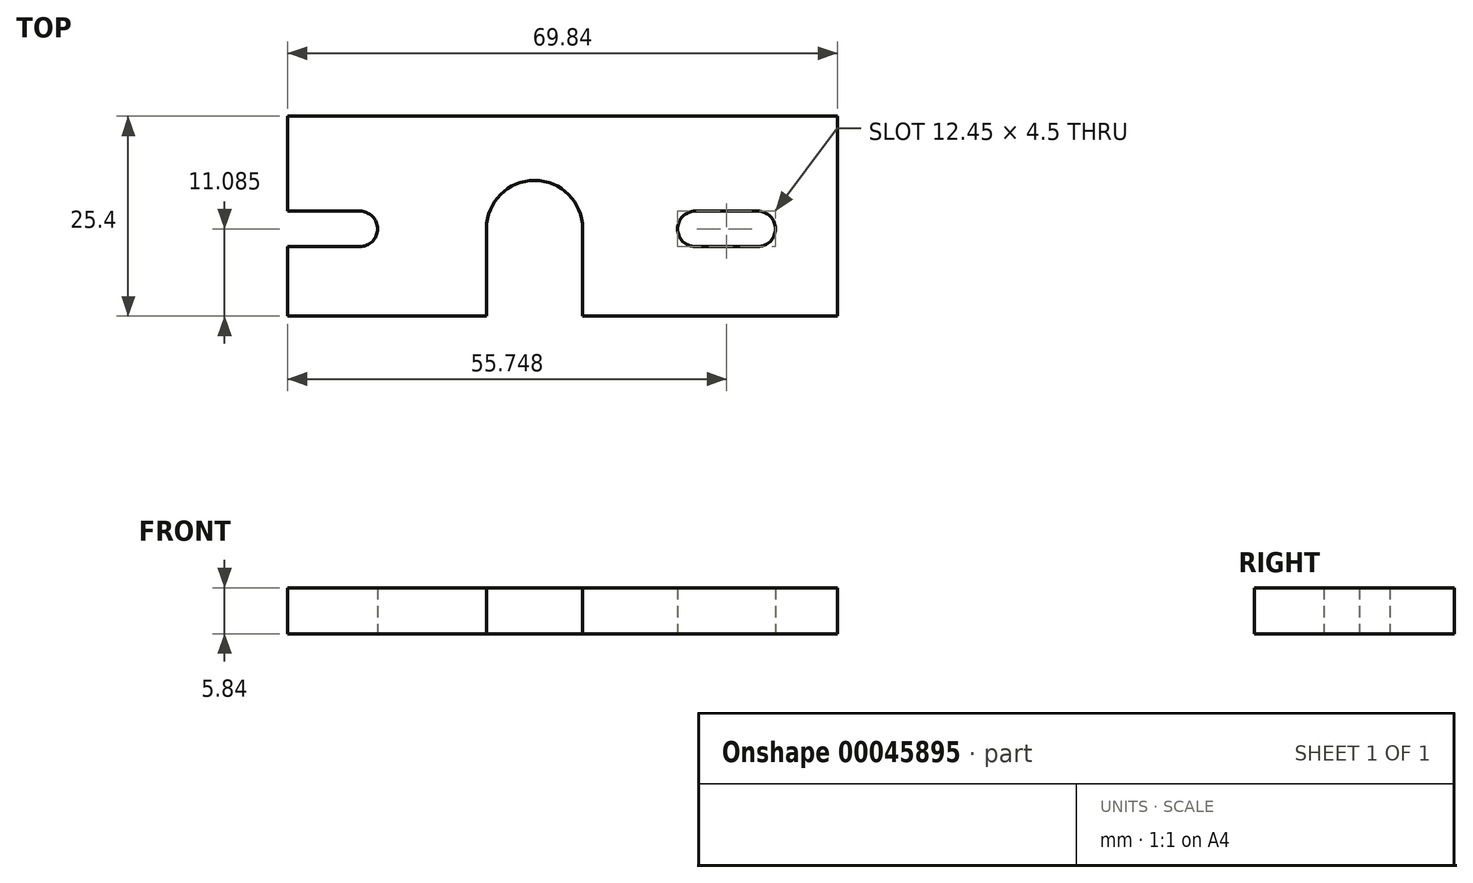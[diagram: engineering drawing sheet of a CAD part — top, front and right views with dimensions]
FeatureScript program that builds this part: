
annotation { "Feature Type Name" : "Feature", "Feature Type Description" : "" }
export const myFeature = defineFeature(function(context is Context, id is Id, definition is map)
    precondition{}
    {
        {
            var Q0;
            Q0=qCreatedBy(makeId("Top.planeOp"),FACE);
            var sketch = newSketch(context, id + "F0", { "sketchPlane" : qUnion([Q0])});
            skLineSegment(sketch, "E0.rect.bottom", {"start": v(34.92, 12.7) * mm, "end": v(-34.93, 12.7) * mm});
            skLineSegment(sketch, "E0.rect.top", {"start": v(34.92, -12.7) * mm, "end": v(-34.93, -12.7) * mm});
            skLineSegment(sketch, "E0.rect.left", {"start": v(34.92, 12.7) * mm, "end": v(34.93, -12.7) * mm});
            skLineSegment(sketch, "E0.rect.right", {"start": v(-34.93, 12.7) * mm, "end": v(-34.93, -12.7) * mm});
            skPoint(sketch, "E0.rect.middle", {"position": v(0, 0) * mm});
            skLineSegment(sketch, "E1", {"start": v(-34.93, 0.64) * mm, "end": v(-25.74, 0.64) * mm});
            skLineSegment(sketch, "E2", {"start": v(-34.92, -3.87) * mm, "end": v(-25.74, -3.87) * mm});
            skArc(sketch, "E3", {"start": v(-25.74, 0.63) * mm, "mid": v(-23.5, -1.62) * mm, "end": v(-25.74, -3.87) * mm});
            skLineSegment(sketch, "E4", {"start": v(24.8, 0.63) * mm, "end": v(16.86, 0.63) * mm});
            skLineSegment(sketch, "E5", {"start": v(24.8, -3.87) * mm, "end": v(16.86, -3.87) * mm});
            skArc(sketch, "E6", {"start": v(16.86, 0.63) * mm, "mid": v(14.6, -1.62) * mm, "end": v(16.86, -3.87) * mm});
            skArc(sketch, "E7", {"start": v(24.8, 0.63) * mm, "mid": v(27.05, -1.62) * mm, "end": v(24.8, -3.87) * mm});
            skCircle(sketch, "E8", {"center": v(-3.56, -1.55) * mm, "radius": 6.1 * mm});
            skLineSegment(sketch, "E9", {"start": v(-9.65, -1.55) * mm, "end": v(-9.65, -12.7) * mm});
            skLineSegment(sketch, "E10", {"start": v(2.54, -1.55) * mm, "end": v(2.54, -12.7) * mm});
            skSolve(sketch);
        }
        {
            var Q0;
            {var subQ7=sQuery(id+"F0.wireOp",EDGE,"E0.rect.bottom");Q0=makeQuery(id+"F0.imprint","IMPRINT",FACE,{"disambiguationData":[TD([[makeQuery(id+"F0.imprint","IMPRINT",EDGE,{"derivedFrom":subQ7}),1.0]])]});}
            extrude(context, id + "F1", {"entities" : qUnion([Q0]), "endBound" : BoundingType.SYMMETRIC, "depth" : 5.84 * mm});
        }
    });
